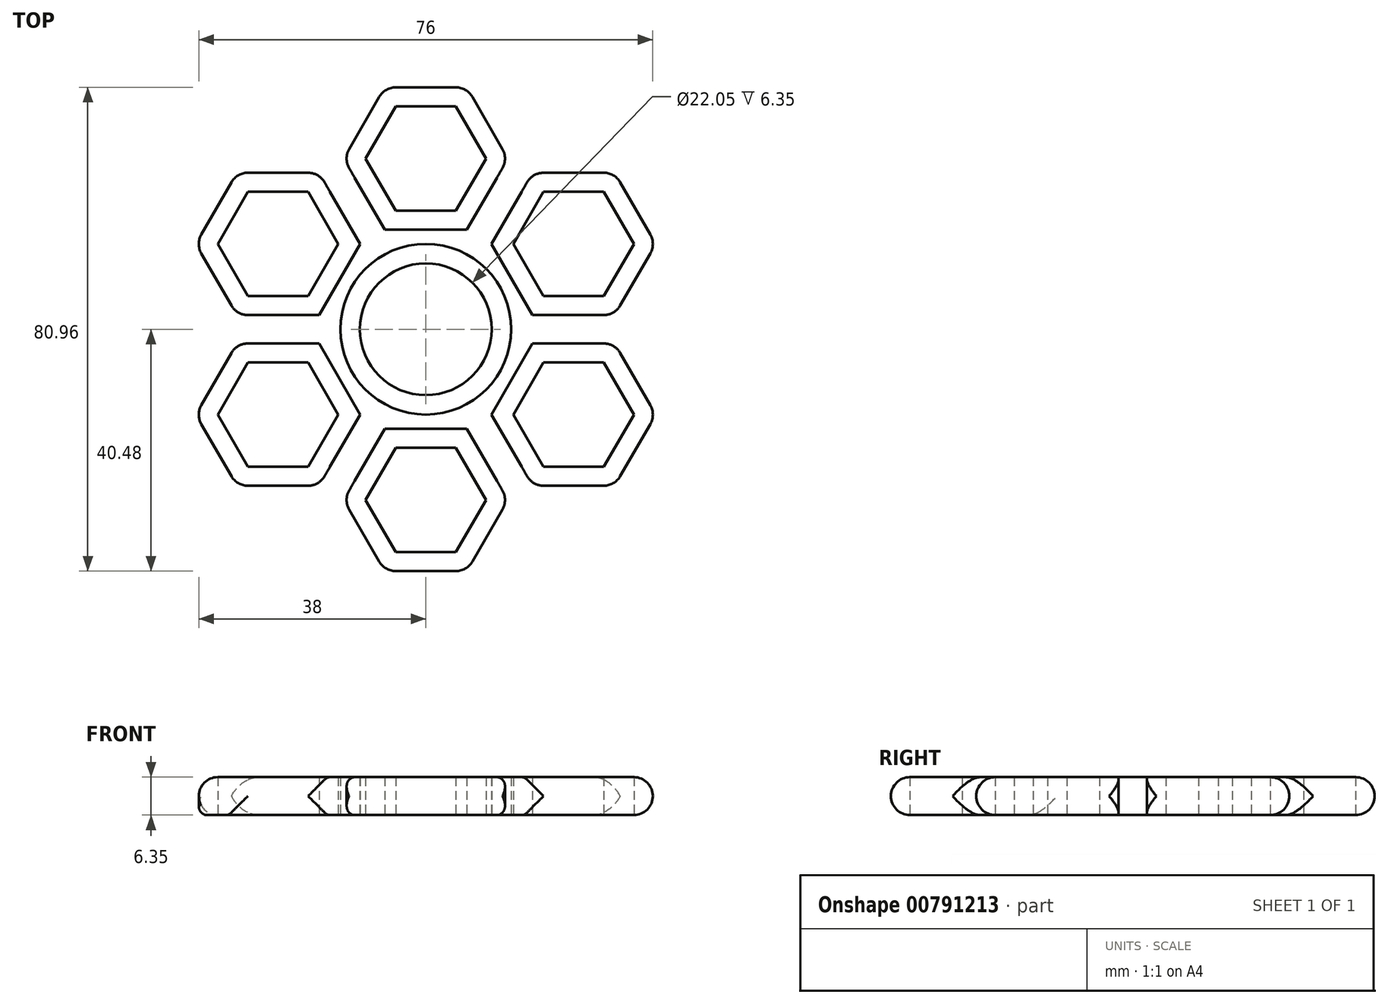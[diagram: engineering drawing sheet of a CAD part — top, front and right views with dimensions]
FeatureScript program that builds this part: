
annotation { "Feature Type Name" : "Feature", "Feature Type Description" : "" }
export const myFeature = defineFeature(function(context is Context, id is Id, definition is map)
    precondition{}
    {
        {
            var Q0;
            Q0=qCreatedBy(makeId("Top.planeOp"),FACE);
            var sketch = newSketch(context, id + "F0", { "sketchPlane" : qUnion([Q0])});
            skCircle(sketch, "E0", {"center": v(0, 0) * mm, "radius": 11.02 * mm});
            skCircle(sketch, "E1", {"center": v(0, 0) * mm, "radius": 14.29 * mm});
            skCircle(sketch, "E2.cCircle", {"center": v(0, 28.58) * mm, "radius": 11.9 * mm, "construction": true});
            skLineSegment(sketch, "E2.0", {"start": v(6.87, 16.67) * mm, "end": v(-6.87, 16.67) * mm});
            skLineSegment(sketch, "E2.1", {"start": v(-6.87, 16.67) * mm, "end": v(-13.75, 28.57) * mm});
            skLineSegment(sketch, "E2.2", {"start": v(-13.75, 28.58) * mm, "end": v(-6.87, 40.48) * mm});
            skLineSegment(sketch, "E2.3", {"start": v(-6.87, 40.48) * mm, "end": v(6.87, 40.48) * mm});
            skLineSegment(sketch, "E2.4", {"start": v(6.87, 40.48) * mm, "end": v(13.75, 28.58) * mm});
            skLineSegment(sketch, "E2.5", {"start": v(13.75, 28.57) * mm, "end": v(6.87, 16.67) * mm});
            skPoint(sketch, "E2.0.midPoint", {"position": v(0, 16.67) * mm});
            skCircle(sketch, "E3.cCircle", {"center": v(0, 28.58) * mm, "radius": 8.73 * mm, "construction": true});
            skLineSegment(sketch, "E3.0", {"start": v(5.04, 19.84) * mm, "end": v(-5.04, 19.84) * mm});
            skLineSegment(sketch, "E3.1", {"start": v(-5.04, 19.84) * mm, "end": v(-10.08, 28.57) * mm});
            skLineSegment(sketch, "E3.2", {"start": v(-10.08, 28.58) * mm, "end": v(-5.04, 37.3) * mm});
            skLineSegment(sketch, "E3.3", {"start": v(-5.04, 37.3) * mm, "end": v(5.04, 37.3) * mm});
            skLineSegment(sketch, "E3.4", {"start": v(5.04, 37.3) * mm, "end": v(10.08, 28.58) * mm});
            skLineSegment(sketch, "E3.5", {"start": v(10.08, 28.57) * mm, "end": v(5.04, 19.84) * mm});
            skPoint(sketch, "E3.0.midPoint", {"position": v(0, 19.84) * mm});
            skLineSegment(sketch, "E4.1.0", {"start": v(-31.62, 2.38) * mm, "end": v(-38.5, 14.29) * mm});
            skLineSegment(sketch, "E4.1.1", {"start": v(-31.62, 26.2) * mm, "end": v(-17.87, 26.2) * mm});
            skLineSegment(sketch, "E4.1.2", {"start": v(-17.87, 26.2) * mm, "end": v(-11, 14.29) * mm});
            skCircle(sketch, "E4.1.3", {"center": v(-24.75, 14.29) * mm, "radius": 8.73 * mm, "construction": true});
            skLineSegment(sketch, "E4.1.4", {"start": v(-29.79, 5.56) * mm, "end": v(-34.83, 14.29) * mm});
            skPoint(sketch, "E4.1.5", {"position": v(-14.44, 8.33) * mm});
            skCircle(sketch, "E4.1.6", {"center": v(-24.75, 14.29) * mm, "radius": 11.9 * mm, "construction": true});
            skPoint(sketch, "E4.1.7", {"position": v(-17.19, 9.92) * mm});
            skLineSegment(sketch, "E4.1.10", {"start": v(-38.5, 14.29) * mm, "end": v(-31.62, 26.2) * mm});
            skLineSegment(sketch, "E4.1.11", {"start": v(-11, 14.29) * mm, "end": v(-17.87, 2.38) * mm});
            skLineSegment(sketch, "E4.1.12", {"start": v(-14.66, 14.29) * mm, "end": v(-19.7, 5.56) * mm});
            skLineSegment(sketch, "E4.1.13", {"start": v(-19.7, 5.56) * mm, "end": v(-29.79, 5.56) * mm});
            skLineSegment(sketch, "E4.1.14", {"start": v(-17.87, 2.38) * mm, "end": v(-31.62, 2.38) * mm});
            skLineSegment(sketch, "E4.1.15", {"start": v(-19.7, 23.02) * mm, "end": v(-14.66, 14.29) * mm});
            skLineSegment(sketch, "E4.1.16", {"start": v(-29.79, 23.02) * mm, "end": v(-19.7, 23.02) * mm});
            skLineSegment(sketch, "E4.1.17", {"start": v(-34.83, 14.29) * mm, "end": v(-29.79, 23.02) * mm});
            skLineSegment(sketch, "E4.2.0", {"start": v(-17.87, -26.2) * mm, "end": v(-31.62, -26.2) * mm});
            skLineSegment(sketch, "E4.2.1", {"start": v(-38.5, -14.29) * mm, "end": v(-31.62, -2.38) * mm});
            skLineSegment(sketch, "E4.2.2", {"start": v(-31.62, -2.38) * mm, "end": v(-17.87, -2.38) * mm});
            skCircle(sketch, "E4.2.3", {"center": v(-24.75, -14.29) * mm, "radius": 8.73 * mm, "construction": true});
            skLineSegment(sketch, "E4.2.4", {"start": v(-19.7, -23.02) * mm, "end": v(-29.79, -23.02) * mm});
            skPoint(sketch, "E4.2.5", {"position": v(-14.44, -8.33) * mm});
            skCircle(sketch, "E4.2.6", {"center": v(-24.75, -14.29) * mm, "radius": 11.9 * mm, "construction": true});
            skPoint(sketch, "E4.2.7", {"position": v(-17.19, -9.92) * mm});
            skLineSegment(sketch, "E4.2.10", {"start": v(-31.62, -26.2) * mm, "end": v(-38.5, -14.29) * mm});
            skLineSegment(sketch, "E4.2.11", {"start": v(-17.87, -2.38) * mm, "end": v(-11, -14.29) * mm});
            skLineSegment(sketch, "E4.2.12", {"start": v(-19.7, -5.56) * mm, "end": v(-14.66, -14.29) * mm});
            skLineSegment(sketch, "E4.2.13", {"start": v(-14.66, -14.29) * mm, "end": v(-19.7, -23.02) * mm});
            skLineSegment(sketch, "E4.2.14", {"start": v(-11, -14.29) * mm, "end": v(-17.87, -26.2) * mm});
            skLineSegment(sketch, "E4.2.15", {"start": v(-29.79, -5.56) * mm, "end": v(-19.7, -5.56) * mm});
            skLineSegment(sketch, "E4.2.16", {"start": v(-34.83, -14.29) * mm, "end": v(-29.79, -5.56) * mm});
            skLineSegment(sketch, "E4.2.17", {"start": v(-29.79, -23.02) * mm, "end": v(-34.83, -14.29) * mm});
            skLineSegment(sketch, "E4.3.0", {"start": v(13.75, -28.58) * mm, "end": v(6.87, -40.48) * mm});
            skLineSegment(sketch, "E4.3.1", {"start": v(-6.87, -40.48) * mm, "end": v(-13.75, -28.58) * mm});
            skLineSegment(sketch, "E4.3.2", {"start": v(-13.75, -28.57) * mm, "end": v(-6.87, -16.67) * mm});
            skCircle(sketch, "E4.3.3", {"center": v(0, -28.58) * mm, "radius": 8.73 * mm, "construction": true});
            skLineSegment(sketch, "E4.3.4", {"start": v(10.08, -28.58) * mm, "end": v(5.04, -37.3) * mm});
            skPoint(sketch, "E4.3.5", {"position": v(0, -16.67) * mm});
            skCircle(sketch, "E4.3.6", {"center": v(0, -28.58) * mm, "radius": 11.9 * mm, "construction": true});
            skPoint(sketch, "E4.3.7", {"position": v(0, -19.84) * mm});
            skLineSegment(sketch, "E4.3.10", {"start": v(6.87, -40.48) * mm, "end": v(-6.87, -40.48) * mm});
            skLineSegment(sketch, "E4.3.11", {"start": v(-6.87, -16.67) * mm, "end": v(6.87, -16.67) * mm});
            skLineSegment(sketch, "E4.3.12", {"start": v(-5.04, -19.84) * mm, "end": v(5.04, -19.84) * mm});
            skLineSegment(sketch, "E4.3.13", {"start": v(5.04, -19.84) * mm, "end": v(10.08, -28.57) * mm});
            skLineSegment(sketch, "E4.3.14", {"start": v(6.87, -16.67) * mm, "end": v(13.75, -28.57) * mm});
            skLineSegment(sketch, "E4.3.15", {"start": v(-10.08, -28.57) * mm, "end": v(-5.04, -19.84) * mm});
            skLineSegment(sketch, "E4.3.16", {"start": v(-5.04, -37.3) * mm, "end": v(-10.08, -28.58) * mm});
            skLineSegment(sketch, "E4.3.17", {"start": v(5.04, -37.3) * mm, "end": v(-5.04, -37.3) * mm});
            skLineSegment(sketch, "E4.4.0", {"start": v(31.62, -2.38) * mm, "end": v(38.5, -14.29) * mm});
            skLineSegment(sketch, "E4.4.1", {"start": v(31.62, -26.2) * mm, "end": v(17.87, -26.2) * mm});
            skLineSegment(sketch, "E4.4.2", {"start": v(17.87, -26.2) * mm, "end": v(11, -14.29) * mm});
            skCircle(sketch, "E4.4.3", {"center": v(24.75, -14.29) * mm, "radius": 8.73 * mm, "construction": true});
            skLineSegment(sketch, "E4.4.4", {"start": v(29.79, -5.56) * mm, "end": v(34.83, -14.29) * mm});
            skPoint(sketch, "E4.4.5", {"position": v(14.44, -8.33) * mm});
            skCircle(sketch, "E4.4.6", {"center": v(24.75, -14.29) * mm, "radius": 11.9 * mm, "construction": true});
            skPoint(sketch, "E4.4.7", {"position": v(17.19, -9.92) * mm});
            skLineSegment(sketch, "E4.4.10", {"start": v(38.5, -14.29) * mm, "end": v(31.62, -26.2) * mm});
            skLineSegment(sketch, "E4.4.11", {"start": v(11, -14.29) * mm, "end": v(17.87, -2.38) * mm});
            skLineSegment(sketch, "E4.4.12", {"start": v(14.66, -14.29) * mm, "end": v(19.7, -5.56) * mm});
            skLineSegment(sketch, "E4.4.13", {"start": v(19.7, -5.56) * mm, "end": v(29.79, -5.56) * mm});
            skLineSegment(sketch, "E4.4.14", {"start": v(17.87, -2.38) * mm, "end": v(31.62, -2.38) * mm});
            skLineSegment(sketch, "E4.4.15", {"start": v(19.7, -23.02) * mm, "end": v(14.66, -14.29) * mm});
            skLineSegment(sketch, "E4.4.16", {"start": v(29.79, -23.02) * mm, "end": v(19.7, -23.02) * mm});
            skLineSegment(sketch, "E4.4.17", {"start": v(34.83, -14.29) * mm, "end": v(29.79, -23.02) * mm});
            skLineSegment(sketch, "E4.5.0", {"start": v(17.87, 26.2) * mm, "end": v(31.62, 26.2) * mm});
            skLineSegment(sketch, "E4.5.1", {"start": v(38.5, 14.29) * mm, "end": v(31.62, 2.38) * mm});
            skLineSegment(sketch, "E4.5.2", {"start": v(31.62, 2.38) * mm, "end": v(17.87, 2.38) * mm});
            skCircle(sketch, "E4.5.3", {"center": v(24.75, 14.29) * mm, "radius": 8.73 * mm, "construction": true});
            skLineSegment(sketch, "E4.5.4", {"start": v(19.7, 23.02) * mm, "end": v(29.79, 23.02) * mm});
            skPoint(sketch, "E4.5.5", {"position": v(14.44, 8.33) * mm});
            skCircle(sketch, "E4.5.6", {"center": v(24.75, 14.29) * mm, "radius": 11.9 * mm, "construction": true});
            skPoint(sketch, "E4.5.7", {"position": v(17.19, 9.92) * mm});
            skLineSegment(sketch, "E4.5.10", {"start": v(31.62, 26.2) * mm, "end": v(38.5, 14.29) * mm});
            skLineSegment(sketch, "E4.5.11", {"start": v(17.87, 2.38) * mm, "end": v(11, 14.29) * mm});
            skLineSegment(sketch, "E4.5.12", {"start": v(19.7, 5.56) * mm, "end": v(14.66, 14.29) * mm});
            skLineSegment(sketch, "E4.5.13", {"start": v(14.66, 14.29) * mm, "end": v(19.7, 23.02) * mm});
            skLineSegment(sketch, "E4.5.14", {"start": v(11, 14.29) * mm, "end": v(17.87, 26.2) * mm});
            skLineSegment(sketch, "E4.5.15", {"start": v(29.79, 5.56) * mm, "end": v(19.7, 5.56) * mm});
            skLineSegment(sketch, "E4.5.16", {"start": v(34.83, 14.29) * mm, "end": v(29.79, 5.56) * mm});
            skLineSegment(sketch, "E4.5.17", {"start": v(29.79, 23.02) * mm, "end": v(34.83, 14.29) * mm});
            skSolve(sketch);
        }
        {
            var Q0;
            Q0=qCreatedBy(makeId("Top.planeOp"),FACE);
            var sketch = newSketch(context, id + "F1", { "sketchPlane" : qUnion([Q0])});
            skCircle(sketch, "E5.0", {"center": v(24.75, 14.29) * mm, "radius": 8.73 * mm});
            skCircle(sketch, "E5.1", {"center": v(24.75, -14.29) * mm, "radius": 8.73 * mm});
            skCircle(sketch, "E5.2", {"center": v(-24.75, -14.29) * mm, "radius": 8.73 * mm});
            skCircle(sketch, "E5.3", {"center": v(0, -28.58) * mm, "radius": 8.73 * mm});
            skCircle(sketch, "E5.4", {"center": v(-24.75, 14.29) * mm, "radius": 8.73 * mm});
            skLineSegment(sketch, "E5.5", {"start": v(5.04, -19.84) * mm, "end": v(10.08, -28.57) * mm});
            skLineSegment(sketch, "E5.6", {"start": v(-14.66, -14.29) * mm, "end": v(-19.7, -23.02) * mm});
            skLineSegment(sketch, "E5.7", {"start": v(-19.7, 5.56) * mm, "end": v(-29.79, 5.56) * mm});
            skLineSegment(sketch, "E5.8", {"start": v(14.66, 14.29) * mm, "end": v(19.7, 23.02) * mm});
            skLineSegment(sketch, "E5.9", {"start": v(19.7, -5.56) * mm, "end": v(29.79, -5.56) * mm});
            skLineSegment(sketch, "E5.10", {"start": v(-29.79, 5.56) * mm, "end": v(-34.83, 14.29) * mm});
            skLineSegment(sketch, "E5.11", {"start": v(19.7, 23.02) * mm, "end": v(29.79, 23.02) * mm});
            skLineSegment(sketch, "E5.12", {"start": v(19.7, -23.02) * mm, "end": v(14.66, -14.29) * mm});
            skLineSegment(sketch, "E5.13", {"start": v(-10.08, -28.57) * mm, "end": v(-5.04, -19.84) * mm});
            skLineSegment(sketch, "E5.14", {"start": v(29.79, -5.56) * mm, "end": v(34.83, -14.29) * mm});
            skLineSegment(sketch, "E5.15", {"start": v(-29.79, -5.56) * mm, "end": v(-19.7, -5.56) * mm});
            skLineSegment(sketch, "E5.16", {"start": v(10.08, -28.58) * mm, "end": v(5.04, -37.3) * mm});
            skLineSegment(sketch, "E5.17", {"start": v(-19.7, -23.02) * mm, "end": v(-29.79, -23.02) * mm});
            skLineSegment(sketch, "E5.18", {"start": v(-19.7, 23.02) * mm, "end": v(-14.66, 14.29) * mm});
            skLineSegment(sketch, "E5.19", {"start": v(29.79, 5.56) * mm, "end": v(19.7, 5.56) * mm});
            skLineSegment(sketch, "E5.20", {"start": v(6.87, -16.67) * mm, "end": v(13.75, -28.57) * mm});
            skLineSegment(sketch, "E5.21", {"start": v(-11, -14.29) * mm, "end": v(-17.87, -26.2) * mm});
            skLineSegment(sketch, "E5.22", {"start": v(-17.87, 2.38) * mm, "end": v(-31.62, 2.38) * mm});
            skLineSegment(sketch, "E5.23", {"start": v(11, 14.29) * mm, "end": v(17.87, 26.2) * mm});
            skLineSegment(sketch, "E5.24", {"start": v(17.87, -2.38) * mm, "end": v(31.62, -2.38) * mm});
            skCircle(sketch, "E5.25", {"center": v(-24.75, 14.29) * mm, "radius": 11.9 * mm});
            skLineSegment(sketch, "E5.26", {"start": v(29.79, -23.02) * mm, "end": v(19.7, -23.02) * mm});
            skCircle(sketch, "E5.27", {"center": v(24.75, 14.29) * mm, "radius": 11.9 * mm});
            skCircle(sketch, "E5.28", {"center": v(24.75, -14.29) * mm, "radius": 11.9 * mm});
            skLineSegment(sketch, "E5.29", {"start": v(-5.04, -37.3) * mm, "end": v(-10.08, -28.58) * mm});
            skCircle(sketch, "E5.30", {"center": v(0, -28.58) * mm, "radius": 11.9 * mm});
            skLineSegment(sketch, "E5.31", {"start": v(-34.83, -14.29) * mm, "end": v(-29.79, -5.56) * mm});
            skLineSegment(sketch, "E5.32", {"start": v(-29.79, 23.02) * mm, "end": v(-19.7, 23.02) * mm});
            skCircle(sketch, "E5.33", {"center": v(-24.75, -14.29) * mm, "radius": 11.9 * mm});
            skLineSegment(sketch, "E5.34", {"start": v(34.83, 14.29) * mm, "end": v(29.79, 5.56) * mm});
            skLineSegment(sketch, "E5.35", {"start": v(34.83, -14.29) * mm, "end": v(29.79, -23.02) * mm});
            skLineSegment(sketch, "E5.36", {"start": v(5.04, -37.3) * mm, "end": v(-5.04, -37.3) * mm});
            skLineSegment(sketch, "E5.37", {"start": v(-29.79, -23.02) * mm, "end": v(-34.83, -14.29) * mm});
            skLineSegment(sketch, "E5.38", {"start": v(-34.83, 14.29) * mm, "end": v(-29.79, 23.02) * mm});
            skLineSegment(sketch, "E5.39", {"start": v(29.79, 23.02) * mm, "end": v(34.83, 14.29) * mm});
            skLineSegment(sketch, "E5.40", {"start": v(-5.04, 37.3) * mm, "end": v(5.04, 37.3) * mm});
            skLineSegment(sketch, "E5.41", {"start": v(5.04, 37.3) * mm, "end": v(10.08, 28.58) * mm});
            skLineSegment(sketch, "E5.42", {"start": v(10.08, 28.57) * mm, "end": v(5.04, 19.84) * mm});
            skCircle(sketch, "E5.43", {"center": v(0, 0) * mm, "radius": 11.02 * mm});
            skCircle(sketch, "E5.44", {"center": v(0, 0) * mm, "radius": 14.29 * mm});
            skCircle(sketch, "E5.45", {"center": v(0, 28.58) * mm, "radius": 11.9 * mm});
            skLineSegment(sketch, "E5.46", {"start": v(6.87, 16.67) * mm, "end": v(-6.87, 16.67) * mm});
            skLineSegment(sketch, "E5.47", {"start": v(-6.87, 16.67) * mm, "end": v(-13.75, 28.57) * mm});
            skLineSegment(sketch, "E5.48", {"start": v(-13.75, 28.58) * mm, "end": v(-6.87, 40.48) * mm});
            skLineSegment(sketch, "E5.49", {"start": v(-6.87, 40.48) * mm, "end": v(6.87, 40.48) * mm});
            skLineSegment(sketch, "E5.50", {"start": v(6.87, 40.48) * mm, "end": v(13.75, 28.58) * mm});
            skLineSegment(sketch, "E5.51", {"start": v(13.75, 28.57) * mm, "end": v(6.87, 16.67) * mm});
            skCircle(sketch, "E5.52", {"center": v(0, 28.58) * mm, "radius": 8.73 * mm});
            skLineSegment(sketch, "E5.53", {"start": v(-5.04, 19.84) * mm, "end": v(-10.08, 28.57) * mm});
            skLineSegment(sketch, "E5.54", {"start": v(-10.08, 28.58) * mm, "end": v(-5.04, 37.3) * mm});
            skLineSegment(sketch, "E5.55", {"start": v(-31.62, 2.38) * mm, "end": v(-38.5, 14.29) * mm});
            skLineSegment(sketch, "E5.56", {"start": v(17.87, 26.2) * mm, "end": v(31.62, 26.2) * mm});
            skLineSegment(sketch, "E5.57", {"start": v(31.62, -2.38) * mm, "end": v(38.5, -14.29) * mm});
            skLineSegment(sketch, "E5.58", {"start": v(13.75, -28.58) * mm, "end": v(6.87, -40.48) * mm});
            skLineSegment(sketch, "E5.59", {"start": v(-17.87, -26.2) * mm, "end": v(-31.62, -26.2) * mm});
            skLineSegment(sketch, "E5.60", {"start": v(6.87, -40.48) * mm, "end": v(-6.87, -40.48) * mm});
            skLineSegment(sketch, "E5.61", {"start": v(-31.62, -26.2) * mm, "end": v(-38.5, -14.29) * mm});
            skLineSegment(sketch, "E5.62", {"start": v(-38.5, 14.29) * mm, "end": v(-31.62, 26.2) * mm});
            skLineSegment(sketch, "E5.63", {"start": v(31.62, 26.2) * mm, "end": v(38.5, 14.29) * mm});
            skLineSegment(sketch, "E5.64", {"start": v(38.5, -14.29) * mm, "end": v(31.62, -26.2) * mm});
            skLineSegment(sketch, "E5.65", {"start": v(-31.62, 26.2) * mm, "end": v(-17.87, 26.2) * mm});
            skLineSegment(sketch, "E5.66", {"start": v(38.5, 14.29) * mm, "end": v(31.62, 2.38) * mm});
            skLineSegment(sketch, "E5.67", {"start": v(31.62, -26.2) * mm, "end": v(17.87, -26.2) * mm});
            skLineSegment(sketch, "E5.68", {"start": v(-6.87, -40.48) * mm, "end": v(-13.75, -28.58) * mm});
            skLineSegment(sketch, "E5.69", {"start": v(-38.5, -14.29) * mm, "end": v(-31.62, -2.38) * mm});
            skLineSegment(sketch, "E5.70", {"start": v(-6.87, -16.67) * mm, "end": v(6.87, -16.67) * mm});
            skLineSegment(sketch, "E5.71", {"start": v(-11, 14.29) * mm, "end": v(-17.87, 2.38) * mm});
            skLineSegment(sketch, "E5.72", {"start": v(17.87, 2.38) * mm, "end": v(11, 14.29) * mm});
            skLineSegment(sketch, "E5.73", {"start": v(-17.87, 26.2) * mm, "end": v(-11, 14.29) * mm});
            skLineSegment(sketch, "E5.74", {"start": v(31.62, 2.38) * mm, "end": v(17.87, 2.38) * mm});
            skLineSegment(sketch, "E5.75", {"start": v(17.87, -26.2) * mm, "end": v(11, -14.29) * mm});
            skLineSegment(sketch, "E5.76", {"start": v(-13.75, -28.57) * mm, "end": v(-6.87, -16.67) * mm});
            skLineSegment(sketch, "E5.77", {"start": v(-31.62, -2.38) * mm, "end": v(-17.87, -2.38) * mm});
            skLineSegment(sketch, "E5.78", {"start": v(19.7, 5.56) * mm, "end": v(14.66, 14.29) * mm});
            skLineSegment(sketch, "E5.79", {"start": v(-14.66, 14.29) * mm, "end": v(-19.7, 5.56) * mm});
            skLineSegment(sketch, "E5.80", {"start": v(-5.04, -19.84) * mm, "end": v(5.04, -19.84) * mm});
            skCircle(sketch, "E5.81", {"center": v(0, 0) * mm, "radius": 14.29 * mm});
            skLineSegment(sketch, "E5.82", {"start": v(5.04, 19.84) * mm, "end": v(-5.04, 19.84) * mm});
            skCircle(sketch, "E5.83", {"center": v(0, 0) * mm, "radius": 11.02 * mm});
            skLineSegment(sketch, "E5.84", {"start": v(-17.87, -2.38) * mm, "end": v(-11, -14.29) * mm});
            skLineSegment(sketch, "E5.85", {"start": v(11, -14.29) * mm, "end": v(17.87, -2.38) * mm});
            skCircle(sketch, "E5.86", {"center": v(0, 0) * mm, "radius": 14.29 * mm});
            skCircle(sketch, "E5.87", {"center": v(0, 0) * mm, "radius": 11.02 * mm});
            skCircle(sketch, "E5.88", {"center": v(0, 0) * mm, "radius": 14.29 * mm});
            skCircle(sketch, "E5.89", {"center": v(0, 0) * mm, "radius": 11.02 * mm});
            skCircle(sketch, "E5.90", {"center": v(0, 0) * mm, "radius": 14.29 * mm});
            skCircle(sketch, "E5.91", {"center": v(0, 0) * mm, "radius": 11.02 * mm});
            skCircle(sketch, "E5.92", {"center": v(0, 0) * mm, "radius": 14.29 * mm});
            skCircle(sketch, "E5.93", {"center": v(0, 0) * mm, "radius": 11.02 * mm});
            skLineSegment(sketch, "E6", {"start": v(-13.75, 28.57) * mm, "end": v(-17.87, 26.2) * mm});
            skLineSegment(sketch, "E7", {"start": v(-31.62, 2.38) * mm, "end": v(-31.62, -2.38) * mm});
            skLineSegment(sketch, "E8", {"start": v(-17.87, -26.2) * mm, "end": v(-13.75, -28.58) * mm});
            skLineSegment(sketch, "E9", {"start": v(13.75, -28.57) * mm, "end": v(17.87, -26.2) * mm});
            skLineSegment(sketch, "E10", {"start": v(31.62, -2.38) * mm, "end": v(31.62, 2.38) * mm});
            skLineSegment(sketch, "E11", {"start": v(13.75, 28.58) * mm, "end": v(17.87, 26.2) * mm});
            skSolve(sketch);
        }
        {
            var Q0;
            Q0=makeQuery(id+"F0.imprint","IMPRINT",FACE,{"disambiguationData":[TD([[makeQuery(id+"F0.imprint","IMPRINT",EDGE,{"derivedFrom":sQuery(id+"F0.wireOp",EDGE,"E4.1.0")}),-1.0]])]});
            var Q1;
            Q1=makeQuery(id+"F0.imprint","IMPRINT",FACE,{"disambiguationData":[TD([[makeQuery(id+"F0.imprint","IMPRINT",EDGE,{"derivedFrom":sQuery(id+"F0.wireOp",EDGE,"E2.0")}),-1.0]])]});
            var Q2;
            Q2=makeQuery(id+"F0.imprint","IMPRINT",FACE,{"disambiguationData":[TD([[makeQuery(id+"F0.imprint","IMPRINT",EDGE,{"derivedFrom":sQuery(id+"F0.wireOp",EDGE,"E4.5.0")}),-1.0]])]});
            var Q3;
            Q3=makeQuery(id+"F0.imprint","IMPRINT",FACE,{"disambiguationData":[TD([[makeQuery(id+"F0.imprint","IMPRINT",EDGE,{"derivedFrom":sQuery(id+"F0.wireOp",EDGE,"E4.4.0")}),-1.0]])]});
            var Q4;
            Q4=makeQuery(id+"F0.imprint","IMPRINT",FACE,{"disambiguationData":[TD([[makeQuery(id+"F0.imprint","IMPRINT",EDGE,{"derivedFrom":sQuery(id+"F0.wireOp",EDGE,"E4.3.0")}),-1.0]])]});
            var Q5;
            Q5=makeQuery(id+"F0.imprint","IMPRINT",FACE,{"disambiguationData":[TD([[makeQuery(id+"F0.imprint","IMPRINT",EDGE,{"derivedFrom":sQuery(id+"F0.wireOp",EDGE,"E4.2.0")}),-1.0]])]});
            var Q6;
            Q6=makeQuery(id+"F1.imprint","IMPRINT",FACE,{"disambiguationData":[TD([[makeQuery(id+"F1.imprint","IMPRINT",EDGE,{"derivedFrom":sQuery(id+"F1.wireOp",EDGE,"E5.92")}),-1.0]])]});
            var Q7;
            Q7=makeQuery(id+"F0.imprint","IMPRINT",FACE,{"disambiguationData":[TD([[makeQuery(id+"F0.imprint","IMPRINT",EDGE,{"derivedFrom":sQuery(id+"F0.wireOp",EDGE,"E1")}),1.0]])]});
            extrude(context, id + "F2", {"entities" : qUnion([Q0, Q1, Q2, Q3, Q4, Q5, Q6, Q7]), "depth" : 6.35 * mm, "offsetDistance" : 25.4 * mm});
        }
        {
            var Q0;
            Q0=makeQuery(id+"F2.opExtrude","SWEPT_EDGE",EDGE,{"disambiguationData":[OSD([sQuery(id+"F0.wireOp",EDGE,"E4.3.0"),sQuery(id+"F0.wireOp",EDGE,"E4.3.10")])]});
            var Q1;
            Q1=makeQuery(id+"F2.opExtrude","SWEPT_EDGE",EDGE,{"disambiguationData":[OSD([sQuery(id+"F0.wireOp",EDGE,"E4.3.1"),sQuery(id+"F0.wireOp",EDGE,"E4.3.10")])]});
            var Q2;
            Q2=makeQuery(id+"F2.opExtrude","SWEPT_EDGE",EDGE,{"disambiguationData":[OSD([sQuery(id+"F0.wireOp",EDGE,"E4.3.0"),sQuery(id+"F0.wireOp",EDGE,"E4.3.14")])]});
            var Q3;
            Q3=makeQuery(id+"F2.opExtrude","SWEPT_EDGE",EDGE,{"disambiguationData":[OSD([sQuery(id+"F0.wireOp",EDGE,"E4.4.1"),sQuery(id+"F0.wireOp",EDGE,"E4.4.2")])]});
            var Q4;
            Q4=makeQuery(id+"F2.opExtrude","SWEPT_EDGE",EDGE,{"disambiguationData":[OSD([sQuery(id+"F0.wireOp",EDGE,"E4.4.1"),sQuery(id+"F0.wireOp",EDGE,"E4.4.10")])]});
            var Q5;
            Q5=makeQuery(id+"F2.opExtrude","SWEPT_EDGE",EDGE,{"disambiguationData":[OSD([sQuery(id+"F0.wireOp",EDGE,"E4.4.0"),sQuery(id+"F0.wireOp",EDGE,"E4.4.10")])]});
            var Q6;
            Q6=makeQuery(id+"F2.opExtrude","SWEPT_EDGE",EDGE,{"disambiguationData":[OSD([sQuery(id+"F0.wireOp",EDGE,"E4.4.0"),sQuery(id+"F0.wireOp",EDGE,"E4.4.14")])]});
            var Q7;
            Q7=makeQuery(id+"F2.opExtrude","SWEPT_EDGE",EDGE,{"disambiguationData":[OSD([sQuery(id+"F0.wireOp",EDGE,"E4.5.1"),sQuery(id+"F0.wireOp",EDGE,"E4.5.2")])]});
            var Q8;
            Q8=makeQuery(id+"F2.opExtrude","SWEPT_EDGE",EDGE,{"disambiguationData":[OSD([sQuery(id+"F0.wireOp",EDGE,"E4.5.1"),sQuery(id+"F0.wireOp",EDGE,"E4.5.10")])]});
            var Q9;
            Q9=makeQuery(id+"F2.opExtrude","SWEPT_EDGE",EDGE,{"disambiguationData":[OSD([sQuery(id+"F0.wireOp",EDGE,"E4.5.0"),sQuery(id+"F0.wireOp",EDGE,"E4.5.10")])]});
            var Q10;
            Q10=makeQuery(id+"F2.opExtrude","SWEPT_EDGE",EDGE,{"disambiguationData":[OSD([sQuery(id+"F0.wireOp",EDGE,"E4.5.0"),sQuery(id+"F0.wireOp",EDGE,"E4.5.14")])]});
            var Q11;
            Q11=makeQuery(id+"F2.opExtrude","SWEPT_EDGE",EDGE,{"disambiguationData":[OSD([sQuery(id+"F0.wireOp",EDGE,"E2.4"),sQuery(id+"F0.wireOp",EDGE,"E2.5")])]});
            var Q12;
            Q12=makeQuery(id+"F2.opExtrude","SWEPT_EDGE",EDGE,{"disambiguationData":[OSD([sQuery(id+"F0.wireOp",EDGE,"E2.3"),sQuery(id+"F0.wireOp",EDGE,"E2.4")])]});
            var Q13;
            Q13=makeQuery(id+"F2.opExtrude","SWEPT_EDGE",EDGE,{"disambiguationData":[OSD([sQuery(id+"F0.wireOp",EDGE,"E2.2"),sQuery(id+"F0.wireOp",EDGE,"E2.3")])]});
            var Q14;
            Q14=makeQuery(id+"F2.opExtrude","SWEPT_EDGE",EDGE,{"disambiguationData":[OSD([sQuery(id+"F0.wireOp",EDGE,"E2.1"),sQuery(id+"F0.wireOp",EDGE,"E2.2")])]});
            var Q15;
            Q15=makeQuery(id+"F2.opExtrude","SWEPT_EDGE",EDGE,{"disambiguationData":[OSD([sQuery(id+"F0.wireOp",EDGE,"E4.1.1"),sQuery(id+"F0.wireOp",EDGE,"E4.1.2")])]});
            var Q16;
            Q16=makeQuery(id+"F2.opExtrude","SWEPT_EDGE",EDGE,{"disambiguationData":[OSD([sQuery(id+"F0.wireOp",EDGE,"E4.1.1"),sQuery(id+"F0.wireOp",EDGE,"E4.1.10")])]});
            var Q17;
            Q17=makeQuery(id+"F2.opExtrude","SWEPT_EDGE",EDGE,{"disambiguationData":[OSD([sQuery(id+"F0.wireOp",EDGE,"E4.1.0"),sQuery(id+"F0.wireOp",EDGE,"E4.1.10")])]});
            var Q18;
            Q18=makeQuery(id+"F2.opExtrude","SWEPT_EDGE",EDGE,{"disambiguationData":[OSD([sQuery(id+"F0.wireOp",EDGE,"E4.1.0"),sQuery(id+"F0.wireOp",EDGE,"E4.1.14")])]});
            var Q19;
            Q19=makeQuery(id+"F2.opExtrude","SWEPT_EDGE",EDGE,{"disambiguationData":[OSD([sQuery(id+"F0.wireOp",EDGE,"E4.2.1"),sQuery(id+"F0.wireOp",EDGE,"E4.2.2")])]});
            var Q20;
            Q20=makeQuery(id+"F2.opExtrude","SWEPT_EDGE",EDGE,{"disambiguationData":[OSD([sQuery(id+"F0.wireOp",EDGE,"E4.2.0"),sQuery(id+"F0.wireOp",EDGE,"E4.2.10")])]});
            var Q21;
            Q21=makeQuery(id+"F2.opExtrude","SWEPT_EDGE",EDGE,{"disambiguationData":[OSD([sQuery(id+"F0.wireOp",EDGE,"E4.2.1"),sQuery(id+"F0.wireOp",EDGE,"E4.2.10")])]});
            var Q22;
            Q22=makeQuery(id+"F2.opExtrude","SWEPT_EDGE",EDGE,{"disambiguationData":[OSD([sQuery(id+"F0.wireOp",EDGE,"E4.2.0"),sQuery(id+"F0.wireOp",EDGE,"E4.2.14")])]});
            var Q23;
            Q23=makeQuery(id+"F2.opExtrude","SWEPT_EDGE",EDGE,{"disambiguationData":[OSD([sQuery(id+"F0.wireOp",EDGE,"E4.3.1"),sQuery(id+"F0.wireOp",EDGE,"E4.3.2")])]});
            var Q24;
            Q24=makeQuery(id+"F2.opExtrude","CAP_EDGE",EDGE,{"disambiguationData":[OSD([sQuery(id+"F0.wireOp",EDGE,"E4.2.0")])],"isStart":false});
            var Q25;
            Q25=makeQuery(id+"F2.opExtrude","CAP_EDGE",EDGE,{"disambiguationData":[OSD([sQuery(id+"F0.wireOp",EDGE,"E4.3.10")])],"isStart":false});
            var Q26;
            Q26=makeQuery(id+"F2.opExtrude","CAP_EDGE",EDGE,{"disambiguationData":[OSD([sQuery(id+"F0.wireOp",EDGE,"E4.3.1")])],"isStart":false});
            var Q27;
            Q27=makeQuery(id+"F2.opExtrude","CAP_EDGE",EDGE,{"disambiguationData":[OSD([sQuery(id+"F1.wireOp",EDGE,"E8")])],"isStart":false});
            var Q28;
            Q28=makeQuery(id+"F2.opExtrude","CAP_EDGE",EDGE,{"disambiguationData":[OSD([sQuery(id+"F0.wireOp",EDGE,"E4.2.10")])],"isStart":false});
            var Q29;
            Q29=makeQuery(id+"F2.opExtrude","CAP_EDGE",EDGE,{"disambiguationData":[OSD([sQuery(id+"F0.wireOp",EDGE,"E4.2.1")])],"isStart":false});
            var Q30;
            Q30=makeQuery(id+"F2.opExtrude","CAP_EDGE",EDGE,{"disambiguationData":[OSD([sQuery(id+"F1.wireOp",EDGE,"E7")])],"isStart":false});
            var Q31;
            Q31=makeQuery(id+"F2.opExtrude","CAP_EDGE",EDGE,{"disambiguationData":[OSD([sQuery(id+"F0.wireOp",EDGE,"E4.1.0")])],"isStart":false});
            var Q32;
            Q32=makeQuery(id+"F2.opExtrude","CAP_EDGE",EDGE,{"disambiguationData":[OSD([sQuery(id+"F0.wireOp",EDGE,"E4.1.10")])],"isStart":false});
            var Q33;
            Q33=makeQuery(id+"F2.opExtrude","CAP_EDGE",EDGE,{"disambiguationData":[OSD([sQuery(id+"F0.wireOp",EDGE,"E4.1.1")])],"isStart":false});
            var Q34;
            Q34=makeQuery(id+"F2.opExtrude","CAP_EDGE",EDGE,{"disambiguationData":[OSD([sQuery(id+"F1.wireOp",EDGE,"E6")])],"isStart":false});
            var Q35;
            Q35=makeQuery(id+"F2.opExtrude","CAP_EDGE",EDGE,{"disambiguationData":[OSD([sQuery(id+"F0.wireOp",EDGE,"E2.2")])],"isStart":false});
            var Q36;
            Q36=makeQuery(id+"F2.opExtrude","CAP_EDGE",EDGE,{"disambiguationData":[OSD([sQuery(id+"F0.wireOp",EDGE,"E2.3")])],"isStart":false});
            var Q37;
            Q37=makeQuery(id+"F2.opExtrude","CAP_EDGE",EDGE,{"disambiguationData":[OSD([sQuery(id+"F0.wireOp",EDGE,"E2.4")])],"isStart":false});
            var Q38;
            Q38=makeQuery(id+"F2.opExtrude","CAP_EDGE",EDGE,{"disambiguationData":[OSD([sQuery(id+"F1.wireOp",EDGE,"E11")])],"isStart":false});
            var Q39;
            Q39=makeQuery(id+"F2.opExtrude","CAP_EDGE",EDGE,{"disambiguationData":[OSD([sQuery(id+"F0.wireOp",EDGE,"E4.5.0")])],"isStart":false});
            var Q40;
            Q40=makeQuery(id+"F2.opExtrude","CAP_EDGE",EDGE,{"disambiguationData":[OSD([sQuery(id+"F0.wireOp",EDGE,"E4.5.10")])],"isStart":false});
            var Q41;
            Q41=makeQuery(id+"F2.opExtrude","CAP_EDGE",EDGE,{"disambiguationData":[OSD([sQuery(id+"F0.wireOp",EDGE,"E4.5.1")])],"isStart":false});
            var Q42;
            Q42=makeQuery(id+"F2.opExtrude","CAP_EDGE",EDGE,{"disambiguationData":[OSD([sQuery(id+"F1.wireOp",EDGE,"E10")])],"isStart":false});
            var Q43;
            Q43=makeQuery(id+"F2.opExtrude","CAP_EDGE",EDGE,{"disambiguationData":[OSD([sQuery(id+"F0.wireOp",EDGE,"E4.4.0")])],"isStart":false});
            var Q44;
            Q44=makeQuery(id+"F2.opExtrude","CAP_EDGE",EDGE,{"disambiguationData":[OSD([sQuery(id+"F0.wireOp",EDGE,"E4.4.10")])],"isStart":false});
            var Q45;
            Q45=makeQuery(id+"F2.opExtrude","CAP_EDGE",EDGE,{"disambiguationData":[OSD([sQuery(id+"F0.wireOp",EDGE,"E4.4.1")])],"isStart":false});
            var Q46;
            Q46=makeQuery(id+"F2.opExtrude","CAP_EDGE",EDGE,{"disambiguationData":[OSD([sQuery(id+"F1.wireOp",EDGE,"E9")])],"isStart":false});
            var Q47;
            Q47=makeQuery(id+"F2.opExtrude","CAP_EDGE",EDGE,{"disambiguationData":[OSD([sQuery(id+"F0.wireOp",EDGE,"E4.3.0")])],"isStart":false});
            var Q48;
            Q48=makeQuery(id+"F2.opExtrude","CAP_EDGE",EDGE,{"disambiguationData":[OSD([sQuery(id+"F0.wireOp",EDGE,"E4.3.10")])],"isStart":true});
            var Q49;
            Q49=makeQuery(id+"F2.opExtrude","CAP_EDGE",EDGE,{"disambiguationData":[OSD([sQuery(id+"F0.wireOp",EDGE,"E4.3.0")])],"isStart":true});
            var Q50;
            Q50=makeQuery(id+"F2.opExtrude","CAP_EDGE",EDGE,{"disambiguationData":[OSD([sQuery(id+"F0.wireOp",EDGE,"E4.3.1")])],"isStart":true});
            var Q51;
            Q51=makeQuery(id+"F2.opExtrude","CAP_EDGE",EDGE,{"disambiguationData":[OSD([sQuery(id+"F1.wireOp",EDGE,"E8")])],"isStart":true});
            var Q52;
            Q52=makeQuery(id+"F2.opExtrude","CAP_EDGE",EDGE,{"disambiguationData":[OSD([sQuery(id+"F0.wireOp",EDGE,"E4.2.0")])],"isStart":true});
            var Q53;
            Q53=makeQuery(id+"F2.opExtrude","CAP_EDGE",EDGE,{"disambiguationData":[OSD([sQuery(id+"F0.wireOp",EDGE,"E4.2.1")])],"isStart":true});
            var Q54;
            Q54=makeQuery(id+"F2.opExtrude","CAP_EDGE",EDGE,{"disambiguationData":[OSD([sQuery(id+"F1.wireOp",EDGE,"E7")])],"isStart":true});
            var Q55;
            Q55=makeQuery(id+"F2.opExtrude","CAP_EDGE",EDGE,{"disambiguationData":[OSD([sQuery(id+"F0.wireOp",EDGE,"E4.1.0")])],"isStart":true});
            var Q56;
            Q56=makeQuery(id+"F2.opExtrude","CAP_EDGE",EDGE,{"disambiguationData":[OSD([sQuery(id+"F0.wireOp",EDGE,"E4.1.10")])],"isStart":true});
            var Q57;
            Q57=makeQuery(id+"F2.opExtrude","CAP_EDGE",EDGE,{"disambiguationData":[OSD([sQuery(id+"F0.wireOp",EDGE,"E4.1.1")])],"isStart":true});
            var Q58;
            Q58=makeQuery(id+"F2.opExtrude","CAP_EDGE",EDGE,{"disambiguationData":[OSD([sQuery(id+"F1.wireOp",EDGE,"E6")])],"isStart":true});
            var Q59;
            Q59=makeQuery(id+"F2.opExtrude","CAP_EDGE",EDGE,{"disambiguationData":[OSD([sQuery(id+"F0.wireOp",EDGE,"E2.2")])],"isStart":true});
            var Q60;
            Q60=makeQuery(id+"F2.opExtrude","CAP_EDGE",EDGE,{"disambiguationData":[OSD([sQuery(id+"F0.wireOp",EDGE,"E2.3")])],"isStart":true});
            var Q61;
            Q61=makeQuery(id+"F2.opExtrude","CAP_EDGE",EDGE,{"disambiguationData":[OSD([sQuery(id+"F0.wireOp",EDGE,"E2.4")])],"isStart":true});
            var Q62;
            Q62=makeQuery(id+"F2.opExtrude","CAP_EDGE",EDGE,{"disambiguationData":[OSD([sQuery(id+"F1.wireOp",EDGE,"E11")])],"isStart":true});
            var Q63;
            Q63=makeQuery(id+"F2.opExtrude","CAP_EDGE",EDGE,{"disambiguationData":[OSD([sQuery(id+"F0.wireOp",EDGE,"E4.5.0")])],"isStart":true});
            var Q64;
            Q64=makeQuery(id+"F2.opExtrude","CAP_EDGE",EDGE,{"disambiguationData":[OSD([sQuery(id+"F0.wireOp",EDGE,"E4.5.10")])],"isStart":true});
            var Q65;
            Q65=makeQuery(id+"F2.opExtrude","CAP_EDGE",EDGE,{"disambiguationData":[OSD([sQuery(id+"F0.wireOp",EDGE,"E4.5.1")])],"isStart":true});
            var Q66;
            Q66=makeQuery(id+"F2.opExtrude","CAP_EDGE",EDGE,{"disambiguationData":[OSD([sQuery(id+"F1.wireOp",EDGE,"E10")])],"isStart":true});
            var Q67;
            Q67=makeQuery(id+"F2.opExtrude","CAP_EDGE",EDGE,{"disambiguationData":[OSD([sQuery(id+"F0.wireOp",EDGE,"E4.4.0")])],"isStart":true});
            var Q68;
            Q68=makeQuery(id+"F2.opExtrude","CAP_EDGE",EDGE,{"disambiguationData":[OSD([sQuery(id+"F0.wireOp",EDGE,"E4.4.10")])],"isStart":true});
            var Q69;
            Q69=makeQuery(id+"F2.opExtrude","CAP_EDGE",EDGE,{"disambiguationData":[OSD([sQuery(id+"F0.wireOp",EDGE,"E4.4.1")])],"isStart":true});
            var Q70;
            Q70=makeQuery(id+"F2.opExtrude","CAP_EDGE",EDGE,{"disambiguationData":[OSD([sQuery(id+"F1.wireOp",EDGE,"E9")])],"isStart":true});
            fillet(context, id + "F3", {"entities" : qUnion([Q0, Q1, Q2, Q3, Q4, Q5, Q6, Q7, Q8, Q9, Q10, Q11, Q12, Q13, Q14, Q15, Q16, Q17, Q18, Q19, Q20, Q21, Q22, Q23, Q24, Q25, Q26, Q27, Q28, Q29, Q30, Q31, Q32, Q33, Q34, Q35, Q36, Q37, Q38, Q39, Q40, Q41, Q42, Q43, Q44, Q45, Q46, Q47, Q48, Q49, Q50, Q51, Q52, Q53, Q54, Q55, Q56, Q57, Q58, Q59, Q60, Q61, Q62, Q63, Q64, Q65, Q66, Q67, Q68, Q69, Q70]), "radius" : 3.17 * mm, "tangentPropagation" : true, "allowEdgeOverflow" : false});
        }
    });
